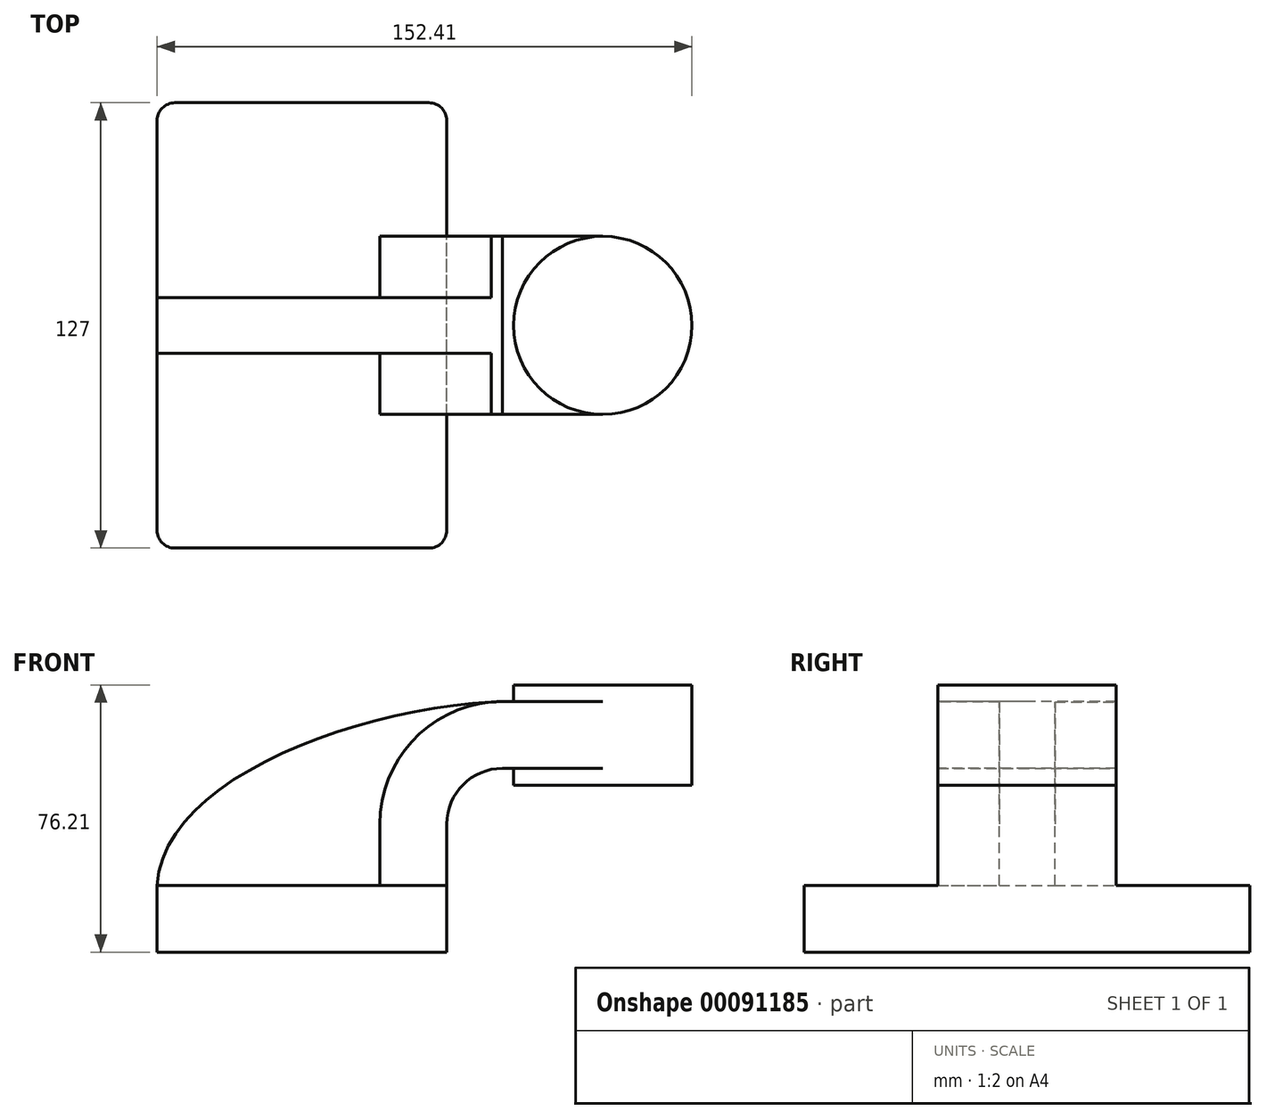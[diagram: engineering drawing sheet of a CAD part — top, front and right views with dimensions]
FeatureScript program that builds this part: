
annotation { "Feature Type Name" : "Feature", "Feature Type Description" : "" }
export const myFeature = defineFeature(function(context is Context, id is Id, definition is map)
    precondition{}
    {
        {
            var Q0;
            Q0=qCreatedBy(makeId("Front.planeOp"),FACE);
            var sketch = newSketch(context, id + "F0", { "sketchPlane" : qUnion([Q0])});
            skLineSegment(sketch, "E0.rect.bottom", {"start": v(-41.28, 9.52) * mm, "end": v(41.28, 9.52) * mm});
            skLineSegment(sketch, "E0.rect.top", {"start": v(-41.28, -9.52) * mm, "end": v(41.28, -9.52) * mm});
            skLineSegment(sketch, "E0.rect.left", {"start": v(-41.28, 9.52) * mm, "end": v(-41.28, -9.52) * mm});
            skLineSegment(sketch, "E0.rect.right", {"start": v(41.28, 9.52) * mm, "end": v(41.28, -9.52) * mm});
            skPoint(sketch, "E0.rect.middle", {"position": v(0, 0) * mm});
            skLineSegment(sketch, "E1", {"start": v(41.28, 9.52) * mm, "end": v(41.28, 27) * mm});
            skArc(sketch, "E2", {"start": v(41.28, 27) * mm, "mid": v(45.92, 38.23) * mm, "end": v(57.15, 42.88) * mm});
            skLineSegment(sketch, "E3", {"start": v(57.15, 42.88) * mm, "end": v(85.72, 42.88) * mm});
            skLineSegment(sketch, "E4.rect.bottom", {"start": v(60.32, 38.1) * mm, "end": v(111.12, 38.1) * mm});
            skLineSegment(sketch, "E4.rect.top", {"start": v(60.32, 66.68) * mm, "end": v(111.12, 66.68) * mm});
            skLineSegment(sketch, "E4.rect.left", {"start": v(60.32, 38.1) * mm, "end": v(60.32, 66.68) * mm});
            skLineSegment(sketch, "E4.rect.right", {"start": v(111.13, 38.1) * mm, "end": v(111.12, 66.68) * mm});
            skPoint(sketch, "E4.rect.middle", {"position": v(85.72, 52.39) * mm});
            skLineSegment(sketch, "E5.0", {"start": v(57.15, 61.93) * mm, "end": v(85.72, 61.93) * mm});
            skArc(sketch, "E5.1", {"start": v(22.23, 27) * mm, "mid": v(32.45, 51.7) * mm, "end": v(57.15, 61.93) * mm});
            skLineSegment(sketch, "E5.2", {"start": v(22.23, 9.52) * mm, "end": v(22.23, 27) * mm});
            skLineSegment(sketch, "E6", {"start": v(85.72, 38.1) * mm, "end": v(85.72, 66.68) * mm});
            skFitSpline(sketch, "E7", {"points": [v(-41.28, 9.53) * mm, v(57.15, 61.93) * mm], "startDerivative": vector(5.2, 92.34) * mm, "endDerivative": vector(120.92, 4.22) * mm});
            skSolve(sketch);
        }
        {
            var Q0;
            Q0=makeQuery(id+"F0.imprint","IMPRINT",FACE,{"disambiguationData":[TD([[makeQuery(id+"F0.imprint","IMPRINT",EDGE,{"derivedFrom":sQuery(id+"F0.wireOp",EDGE,"E0.rect.top")}),1.0]])]});
            extrude(context, id + "F1", {"entities" : qUnion([Q0]), "endBound" : BoundingType.SYMMETRIC, "depth" : 127 * mm});
        }
        {
            var Q0;
            {var subQ9=sQuery(id+"F0.wireOp",EDGE,"E1");Q0=makeQuery(id+"F0.imprint","IMPRINT",FACE,{"disambiguationData":[TD([[makeQuery(id+"F0.imprint","IMPRINT",EDGE,{"derivedFrom":subQ9}),1.0]])]});}
            var Q1;
            {var subQ0=sQuery(id+"F0.wireOp",EDGE,"E6");var subQ1=sQuery(id+"F0.wireOp",EDGE,"E3");var subQ2=makeQuery(id+"F0.imprint","INTERSECT",VERTEX,{"derivedFrom":[subQ1,subQ0]});Q1=makeQuery(id+"F0.imprint","IMPRINT",FACE,{"disambiguationData":[TD([[makeQuery(id+"F0.imprint","IMPRINT",EDGE,{"disambiguationData":[TD([[subQ2,1.0]])],"derivedFrom":subQ1}),1.0]])]});}
            extrude(context, id + "F2", {"entities" : qUnion([Q0, Q1]), "operationType" : NewBodyOperationType.ADD, "endBound" : BoundingType.SYMMETRIC, "depth" : 50.8 * mm});
        }
        {
            var Q0;
            {var subQ3=sQuery(id+"F0.wireOp",EDGE,"E5.2");Q0=makeQuery(id+"F0.imprint","IMPRINT",FACE,{"disambiguationData":[TD([[makeQuery(id+"F0.imprint","IMPRINT",EDGE,{"derivedFrom":subQ3}),1.0]])]});}
            extrude(context, id + "F3", {"entities" : qUnion([Q0]), "operationType" : NewBodyOperationType.ADD, "endBound" : BoundingType.SYMMETRIC, "depth" : 15.88 * mm});
        }
        {
            var Q0;
            {var subQ5=sQuery(id+"F0.wireOp",EDGE,"E4.rect.right");Q0=makeQuery(id+"F0.imprint","IMPRINT",FACE,{"disambiguationData":[TD([[makeQuery(id+"F0.imprint","IMPRINT",EDGE,{"derivedFrom":subQ5}),1.0]])]});}
            var Q1;
            Q1=sQuery(id+"F0.wireOp",EDGE,"E6");
            revolve(context, id + "F4", {"operationType" : NewBodyOperationType.ADD, "entities" : qUnion([Q0]), "axis" : qUnion([Q1]), "revolveType" : RevolveType.FULL});
        }
        {
            var Q0;
            Q0=makeQuery(id+"F1.opExtrude","CAP_EDGE",EDGE,{"disambiguationData":[OSD([sQuery(id+"F0.wireOp",EDGE,"E0.rect.left")])],"isStart":false});
            var Q1;
            Q1=makeQuery(id+"F1.opExtrude","CAP_EDGE",EDGE,{"disambiguationData":[OSD([sQuery(id+"F0.wireOp",EDGE,"E0.rect.right")])],"isStart":false});
            var Q2;
            Q2=makeQuery(id+"F1.opExtrude","CAP_EDGE",EDGE,{"disambiguationData":[OSD([sQuery(id+"F0.wireOp",EDGE,"E0.rect.left")])],"isStart":true});
            var Q3;
            Q3=makeQuery(id+"F1.opExtrude","CAP_EDGE",EDGE,{"disambiguationData":[OSD([sQuery(id+"F0.wireOp",EDGE,"E0.rect.right")])],"isStart":true});
            fillet(context, id + "F5", {"entities" : qUnion([Q0, Q1, Q2, Q3]), "radius" : 6.35 * mm, "tangentPropagation" : true, "allowEdgeOverflow" : false});
        }
        {
            var Q0;
            Q0=makeQuery(id+"F0.imprint","IMPRINT",FACE,{"disambiguationData":[TD([[makeQuery(id+"F0.imprint","IMPRINT",EDGE,{"derivedFrom":sQuery(id+"F0.wireOp",EDGE,"E0.rect.top")}),1.0]])]});
            extrude(context, id + "F6", {"entities" : qUnion([Q0]), "endBound" : BoundingType.SYMMETRIC, "depth" : 127 * mm});
        }
        {
            var Q0;
            {var subQ9=sQuery(id+"F0.wireOp",EDGE,"E1");Q0=makeQuery(id+"F0.imprint","IMPRINT",FACE,{"disambiguationData":[TD([[makeQuery(id+"F0.imprint","IMPRINT",EDGE,{"derivedFrom":subQ9}),1.0]])]});}
            var Q1;
            {var subQ0=sQuery(id+"F0.wireOp",EDGE,"E6");var subQ1=sQuery(id+"F0.wireOp",EDGE,"E3");var subQ2=makeQuery(id+"F0.imprint","INTERSECT",VERTEX,{"derivedFrom":[subQ1,subQ0]});Q1=makeQuery(id+"F0.imprint","IMPRINT",FACE,{"disambiguationData":[TD([[makeQuery(id+"F0.imprint","IMPRINT",EDGE,{"disambiguationData":[TD([[subQ2,1.0]])],"derivedFrom":subQ1}),1.0]])]});}
            extrude(context, id + "F7", {"entities" : qUnion([Q0, Q1]), "operationType" : NewBodyOperationType.ADD, "endBound" : BoundingType.SYMMETRIC, "depth" : 50.8 * mm});
        }
        {
            var Q0;
            {var subQ3=sQuery(id+"F0.wireOp",EDGE,"E5.2");Q0=makeQuery(id+"F0.imprint","IMPRINT",FACE,{"disambiguationData":[TD([[makeQuery(id+"F0.imprint","IMPRINT",EDGE,{"derivedFrom":subQ3}),1.0]])]});}
            extrude(context, id + "F8", {"entities" : qUnion([Q0]), "operationType" : NewBodyOperationType.ADD, "endBound" : BoundingType.SYMMETRIC, "depth" : 15.88 * mm});
        }
        {
            var Q0;
            {var subQ5=sQuery(id+"F0.wireOp",EDGE,"E4.rect.right");Q0=makeQuery(id+"F0.imprint","IMPRINT",FACE,{"disambiguationData":[TD([[makeQuery(id+"F0.imprint","IMPRINT",EDGE,{"derivedFrom":subQ5}),1.0]])]});}
            var Q1;
            Q1=sQuery(id+"F0.wireOp",EDGE,"E6");
            revolve(context, id + "F9", {"operationType" : NewBodyOperationType.ADD, "entities" : qUnion([Q0]), "axis" : qUnion([Q1]), "revolveType" : RevolveType.FULL});
        }
        {
            var Q0;
            Q0=makeQuery(id+"F6.opExtrude","CAP_EDGE",EDGE,{"disambiguationData":[OSD([sQuery(id+"F0.wireOp",EDGE,"E0.rect.right")])],"isStart":false});
            var Q1;
            Q1=makeQuery(id+"F6.opExtrude","CAP_EDGE",EDGE,{"disambiguationData":[OSD([sQuery(id+"F0.wireOp",EDGE,"E0.rect.left")])],"isStart":false});
            var Q2;
            Q2=makeQuery(id+"F6.opExtrude","CAP_EDGE",EDGE,{"disambiguationData":[OSD([sQuery(id+"F0.wireOp",EDGE,"E0.rect.right")])],"isStart":true});
            var Q3;
            Q3=makeQuery(id+"F6.opExtrude","CAP_EDGE",EDGE,{"disambiguationData":[OSD([sQuery(id+"F0.wireOp",EDGE,"E0.rect.left")])],"isStart":true});
            fillet(context, id + "F10", {"entities" : qUnion([Q0, Q1, Q2, Q3]), "radius" : 5.08 * mm, "tangentPropagation" : true, "allowEdgeOverflow" : false});
        }
    });
